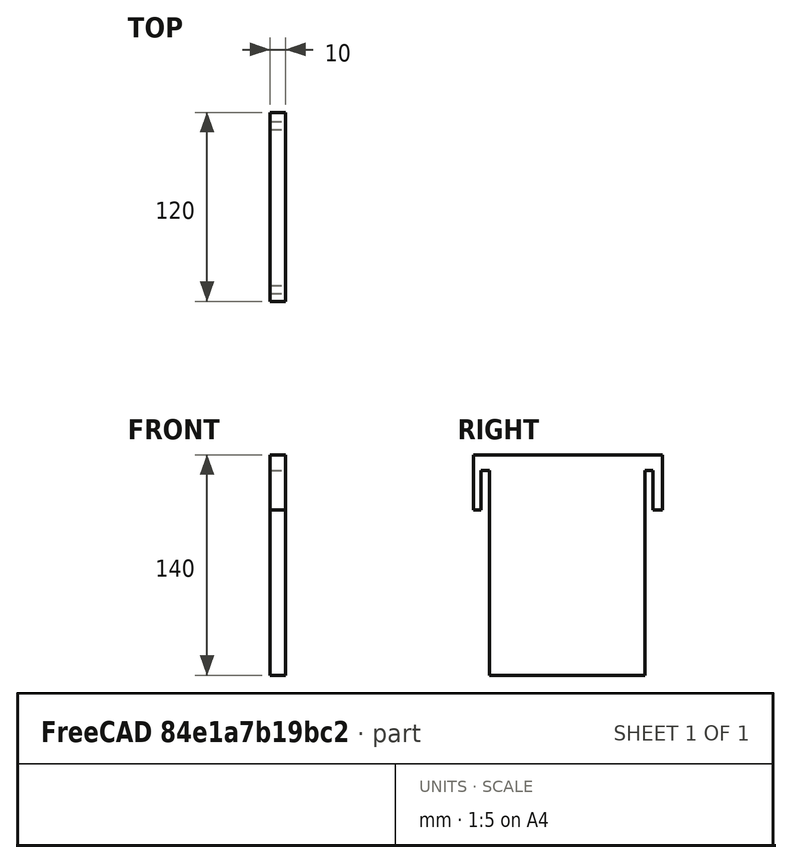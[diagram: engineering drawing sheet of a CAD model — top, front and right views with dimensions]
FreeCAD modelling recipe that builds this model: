
FCSTD DOCUMENT  (FreeCAD 0.17R13522 (Git))
Label: Taller divider
License: All rights reserved
LicenseURL: http://en.wikipedia.org/wiki/All_rights_reserved
objects: Part::Box×4, Part::Cut×2, Part::Fuse×1
note: 7 computed .brp shape members not serialized (recipe doc carries the construction recipe); baked Part::Feature solids carry a one-line shape summary decoded from their .brp

FEATURE [Part::Box] Box003  label="Cube003"
  AttacherType = Attacher::AttachEngine3D
  Height = 25
  Length = 10
  Placement = pos=(0,99,75) rot=(0,0,1;0rad)
  Width = 5.1
FEATURE [Part::Box] Box002  label="Cube002"
  AttacherType = Attacher::AttachEngine3D
  Height = 25
  Length = 10
  Placement = pos=(0,-5.1,75) rot=(0,0,1;0rad)
  Width = 5.1
FEATURE [Part::Box] Box001  label="Cube001"
  AttacherType = Attacher::AttachEngine3D
  Height = 35
  Length = 10
  Placement = pos=(0,-10,75) rot=(0,0,1;0rad)
  Width = 120
FEATURE [Part::Box] Box  label="Cube"
  AttacherType = Attacher::AttachEngine3D
  Height = 140
  Length = 10
  Placement = pos=(0,0,-30) rot=(0,0,1;0rad)
  Width = 99
FEATURE [Part::Cut] Cut
  Base = -> Box001
  Tool = -> Box002
FEATURE [Part::Cut] Cut001
  Base = -> Cut
  Tool = -> Box003
FEATURE [Part::Fuse] Fusion
  Base = -> Box
  Tool = -> Cut001
